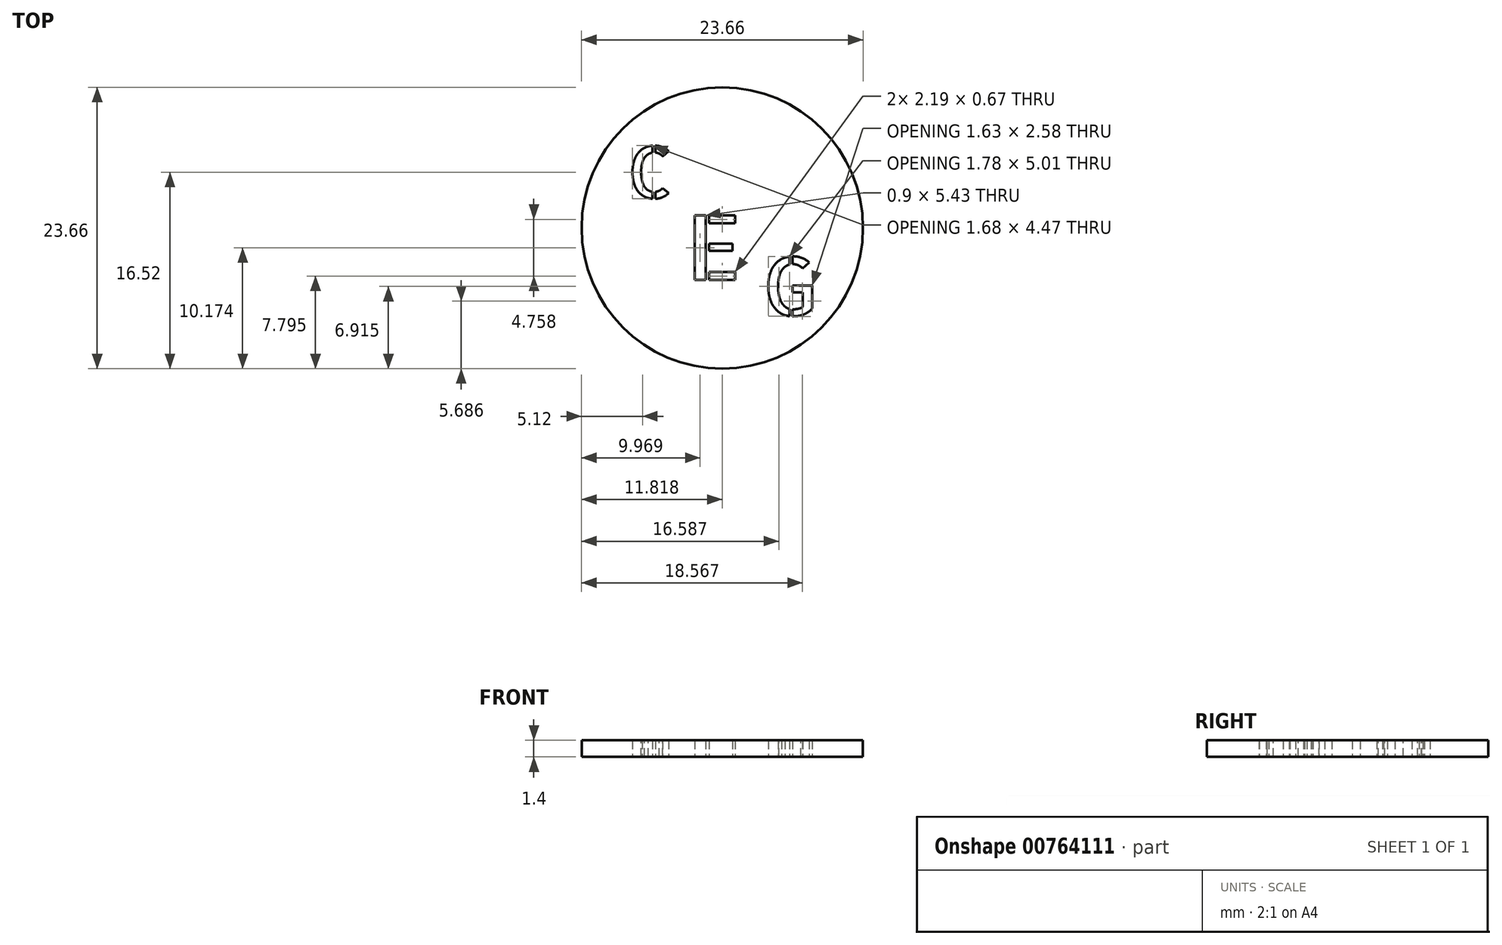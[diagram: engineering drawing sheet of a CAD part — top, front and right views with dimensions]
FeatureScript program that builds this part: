
annotation { "Feature Type Name" : "Feature", "Feature Type Description" : "" }
export const myFeature = defineFeature(function(context is Context, id is Id, definition is map)
    precondition{}
    {
        {
            var Q0;
            Q0=qCreatedBy(makeId("Top.planeOp"),FACE);
            var sketch = newSketch(context, id + "F0", { "sketchPlane" : qUnion([Q0])});
            skCircle(sketch, "E0", {"center": v(0, 0) * mm, "radius": 11.82 * mm});
            skText(sketch, "E1", { "text": "C", "fontName": "AllertaStencil-Regular.ttf"});
            skText(sketch, "E2", { "text": "E", "fontName": "AllertaStencil-Regular.ttf"});
            skText(sketch, "E3", { "text": "G", "fontName": "AllertaStencil-Regular.ttf"});
            const initialGuessF0  = {"E1": [-0.00802, 0.00248, 1, 0, 0.00438], "E2": [-0.00301, -0.00437, 1, 0, 0.00543], "E3": [0.00334, -0.0074, 1, 0, 0.00494]};
            skSetInitialGuess(sketch, initialGuessF0);
            skSolve(sketch);
        }
        {
            var Q0;
            Q0=makeQuery(id+"F0.imprint","IMPRINT",FACE,{"disambiguationData":[TD([[makeQuery(id+"F0.imprint","IMPRINT",EDGE,{"derivedFrom":sQuery(id+"F0.wireOp",EDGE,"E0")}),1.0]])]});
            extrude(context, id + "F1", {"entities" : qUnion([Q0]), "depth" : 1.4 * mm, "offsetDistance" : 25 * mm});
        }
    });
